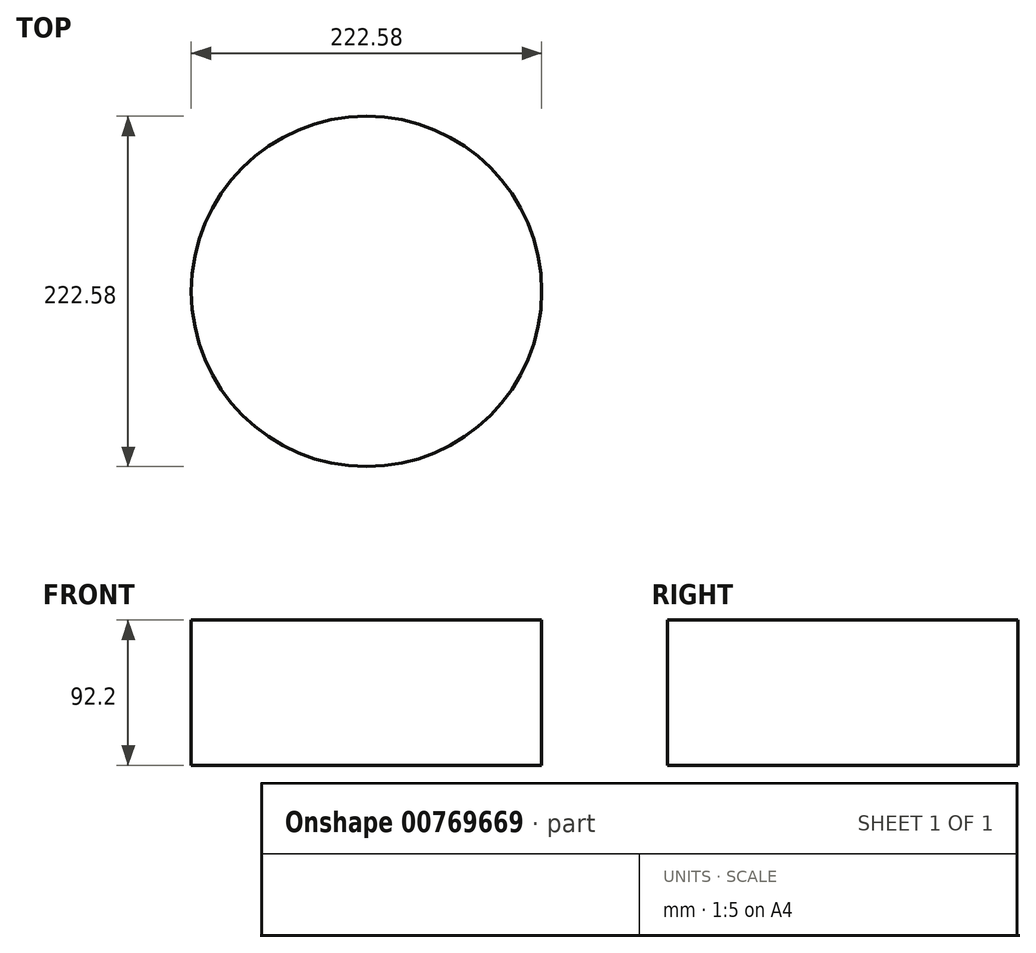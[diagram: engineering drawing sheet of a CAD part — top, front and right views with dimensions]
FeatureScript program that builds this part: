
annotation { "Feature Type Name" : "Feature", "Feature Type Description" : "" }
export const myFeature = defineFeature(function(context is Context, id is Id, definition is map)
    precondition{}
    {
        {
            var Q0;
            Q0=qCreatedBy(makeId("Top.planeOp"),FACE);
            var sketch = newSketch(context, id + "F0", { "sketchPlane" : qUnion([Q0])});
            skCircle(sketch, "E0", {"center": v(0, 0) * mm, "radius": 111.29 * mm});
            skSolve(sketch);
        }
        {
            var Q0;
            Q0=makeQuery(id+"F0.imprint","IMPRINT",FACE,{"disambiguationData":[TD([[makeQuery(id+"F0.imprint","IMPRINT",EDGE,{"derivedFrom":sQuery(id+"F0.wireOp",EDGE,"E0")}),1.0]])]});
            extrude(context, id + "F1", {"entities" : qUnion([Q0]), "depth" : 92.2 * mm, "offsetDistance" : 25.4 * mm});
        }
    });
